# Revit family: 303_R415X_+R470
name_source: partatom
category: Pipe Accessories
revit_build: Autodesk Revit 2018 (Build: 20170223_1515(x64)
units: mm (PartAtom-declared; Revit-internal decimal feet)

## family parameters
Always vertical = Yes
Cut with Voids When Loaded = No
Part Type = Valve - Breaks Into
Round Connector Dimension = Use Diameter
Shared = No
Work Plane-Based = No

## types (3) — shared parameters
CAT0 = Yes
CenSd_W3_6 = 13 mm
D1 = 15 mm
Description = Angle valve  with thermostatic option
G1 = 9 mm  [stored 0.0295276 ft]
J = 36 mm  [stored 0.11811 ft]
J1 = 7 mm  [stored 0.0229659 ft]
J2 = 5 mm  [stored 0.0164042 ft]
J3 = 23 mm
L2D_Min = 3048 mm  [stored 10 ft]
Manufacturer = Giacomini
QmdConnectorList = 301;D;302;D1
TR1 = 20 mm  [stored 0.0656168 ft]
URL = http://www.giacomini.com
W1 = 5 mm  [stored 0.0164042 ft]
W2 = 12 mm  [stored 0.0393701 ft]
W3 = 15 mm  [stored 0.0492126 ft]
W4 = 8 mm  [stored 0.0262467 ft]
Z1 = 10 mm  [stored 0.0328084 ft]
magiPartTypeId = 303
magiProductFamilyId = R415X*+R470
zero-valued in all types: MC_Default_elevation

## per-type parameters (varying)
| type | CenSd_K1_6 | D | K1 | K2 | L1 | L2 | L2D | L5 | L6 | LT1 | LT1__ve | P1 | P2 | R | TH2 | TH2__ve | W2D |
| R415X033+R470 | 11 mm | 15 mm | 13 mm | 10 mm  [stored 0.0328084 ft] | 10 mm  [stored 0.0328084 ft] | 20 mm  [stored 0.0656168 ft] | 40 mm  [stored 0.131234 ft] | 13 mm | 7 mm  [stored 0.0229659 ft] | 21 mm  [stored 0.0688976 ft] | -21 mm  [stored -0.0688976 ft] | No | Yes | 8 mm  [stored 0.0262467 ft] | 86 mm | -86 mm | 15 mm  [stored 0.0492126 ft] |
| R415X043+R470 | 8 mm  [stored 0.0262467 ft] | 18 mm | 9 mm  [stored 0.0295276 ft] | 7 mm  [stored 0.0229659 ft] | 9 mm  [stored 0.0295276 ft] | 17 mm | 34 mm | 11 mm | 6 mm  [stored 0.019685 ft] | 19 mm | -19 mm | Yes | No | 9 mm  [stored 0.0295276 ft] | 82 mm | -82 mm | 18 mm  [stored 0.0590551 ft] |
| R415X042+R470 | 7 mm  [stored 0.0229659 ft] | 16 mm | 8 mm  [stored 0.0262467 ft] | 6 mm  [stored 0.019685 ft] | 9 mm  [stored 0.0295276 ft] | 17 mm | 34 mm | 11 mm | 6 mm  [stored 0.019685 ft] | 19 mm | -19 mm | Yes | No | 8 mm  [stored 0.0262467 ft] | 82 mm | -82 mm | 16 mm |

note: column(s) folded — value = type name in every type: magiProductCode, magiProductId

note: [stored X ft] marks values corroborated as IEEE doubles in the binary element streams (Revit-internal decimal feet)

## geometry (parser evidence)
native form markers: Sweep x1
no freeform markers — native parametric forms only
